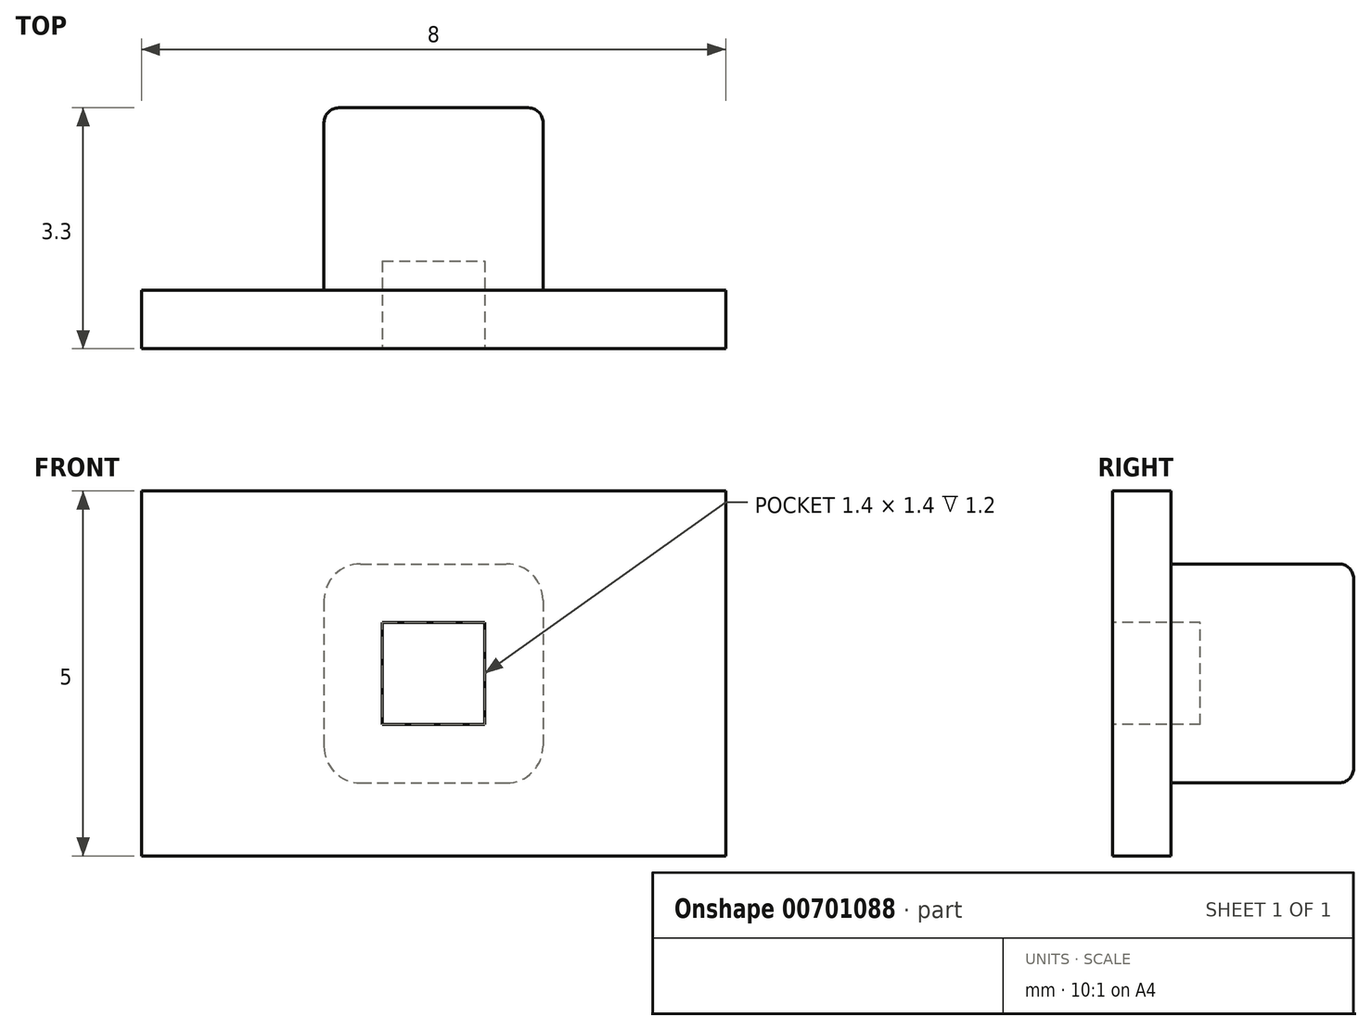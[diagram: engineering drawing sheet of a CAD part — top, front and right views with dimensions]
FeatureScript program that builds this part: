
annotation { "Feature Type Name" : "Feature", "Feature Type Description" : "" }
export const myFeature = defineFeature(function(context is Context, id is Id, definition is map)
    precondition{}
    {
        {
            var Q0;
            Q0=qCreatedBy(makeId("Top.planeOp"),FACE);
            var sketch = newSketch(context, id + "F0", { "sketchPlane" : qUnion([Q0])});
            skLineSegment(sketch, "E0.bottom", {"start": v(0, 0) * mm, "end": v(8, 0) * mm});
            skLineSegment(sketch, "E0.top", {"start": v(0, 0.8) * mm, "end": v(2.5, 0.8) * mm});
            skLineSegment(sketch, "E0.left", {"start": v(0, 0) * mm, "end": v(0, 0.8) * mm});
            skLineSegment(sketch, "E0.right", {"start": v(8, 0) * mm, "end": v(8, 0.8) * mm});
            skLineSegment(sketch, "E1", {"start": v(2.5, 0.8) * mm, "end": v(2.5, 3.3) * mm});
            skLineSegment(sketch, "E2", {"start": v(2.5, 3.3) * mm, "end": v(5.5, 3.3) * mm});
            skLineSegment(sketch, "E3", {"start": v(5.5, 3.3) * mm, "end": v(5.5, 0.8) * mm});
            skLineSegment(sketch, "E4.trimOffspring", {"start": v(5.5, 0.8) * mm, "end": v(8, 0.8) * mm});
            skSolve(sketch);
        }
        {
            var Q0;
            Q0 = qSketchRegion(id + "F0", true);
            extrude(context, id + "F1", {"entities" : qUnion([Q0]), "depth" : 3 * mm, "offsetDistance" : 25 * mm});
        }
        {
            var Q0;
            Q0=makeQuery(id+"F1.opExtrude","SWEPT_FACE",FACE,{"disambiguationData":[OSD([sQuery(id+"F0.wireOp",EDGE,"E0.bottom")])]});
            var sketch = newSketch(context, id + "F2", { "sketchPlane" : qUnion([Q0])});
            skLineSegment(sketch, "E5.bottom", {"start": v(3.3, 0.8) * mm, "end": v(4.7, 0.8) * mm});
            skLineSegment(sketch, "E5.top", {"start": v(3.3, 2.2) * mm, "end": v(4.7, 2.2) * mm});
            skLineSegment(sketch, "E5.left", {"start": v(3.3, 0.8) * mm, "end": v(3.3, 2.2) * mm});
            skLineSegment(sketch, "E5.right", {"start": v(4.7, 0.8) * mm, "end": v(4.7, 2.2) * mm});
            skLineSegment(sketch, "E6", {"start": v(0, 1.5) * mm, "end": v(1.82, 1.5) * mm, "construction": true});
            skLineSegment(sketch, "E7", {"start": v(4, 0) * mm, "end": v(4, 0.82) * mm, "construction": true});
            skSolve(sketch);
        }
        {
            var Q0;
            Q0 = qSketchRegion(id + "F2", true);
            extrude(context, id + "F3", {"entities" : qUnion([Q0]), "operationType" : NewBodyOperationType.REMOVE, "oppositeDirection" : true, "depth" : 1.2 * mm, "offsetDistance" : 25 * mm});
        }
        {
            var Q0;
            Q0=makeQuery(id+"F1.opExtrude","CAP_EDGE",EDGE,{"disambiguationData":[OSD([sQuery(id+"F0.wireOp",EDGE,"E3")])],"isStart":false});
            var Q1;
            Q1=makeQuery(id+"F1.opExtrude","CAP_EDGE",EDGE,{"disambiguationData":[OSD([sQuery(id+"F0.wireOp",EDGE,"E1")])],"isStart":false});
            var Q2;
            Q2=makeQuery(id+"F1.opExtrude","CAP_EDGE",EDGE,{"disambiguationData":[OSD([sQuery(id+"F0.wireOp",EDGE,"E1")])],"isStart":true});
            var Q3;
            Q3=makeQuery(id+"F1.opExtrude","CAP_EDGE",EDGE,{"disambiguationData":[OSD([sQuery(id+"F0.wireOp",EDGE,"E3")])],"isStart":true});
            fillet(context, id + "F4", {"entities" : qUnion([Q0, Q1, Q2, Q3]), "radius" : 0.5 * mm, "tangentPropagation" : true, "allowEdgeOverflow" : false});
        }
        {
            var Q0;
            Q0=makeQuery(id+"F1.opExtrude","CAP_EDGE",EDGE,{"disambiguationData":[OSD([sQuery(id+"F0.wireOp",EDGE,"E2")])],"isStart":false});
            var Q1;
            Q1=makeQuery(id+"F4.opFillet","BLEND_EDGE",EDGE,{"blendedFrom":[makeQuery(id+"F1.opExtrude","CAP_EDGE",EDGE,{"disambiguationData":[OSD([sQuery(id+"F0.wireOp",EDGE,"E3")])],"isStart":false}),makeQuery(id+"F1.opExtrude","SWEPT_FACE",FACE,{"disambiguationData":[OSD([sQuery(id+"F0.wireOp",EDGE,"E2")])]})],"blendedInto":[makeQuery(id+"F1.opExtrude","SWEPT_FACE",FACE,{"disambiguationData":[OSD([sQuery(id+"F0.wireOp",EDGE,"E2")])]})]});
            var Q2;
            Q2=makeQuery(id+"F1.opExtrude","SWEPT_EDGE",EDGE,{"disambiguationData":[OSD([sQuery(id+"F0.wireOp",EDGE,"E2"),sQuery(id+"F0.wireOp",EDGE,"E3")])]});
            var Q3;
            Q3=makeQuery(id+"F4.opFillet","BLEND_EDGE",EDGE,{"blendedFrom":[makeQuery(id+"F1.opExtrude","CAP_EDGE",EDGE,{"disambiguationData":[OSD([sQuery(id+"F0.wireOp",EDGE,"E3")])],"isStart":true}),makeQuery(id+"F1.opExtrude","SWEPT_FACE",FACE,{"disambiguationData":[OSD([sQuery(id+"F0.wireOp",EDGE,"E2")])]})],"blendedInto":[makeQuery(id+"F1.opExtrude","SWEPT_FACE",FACE,{"disambiguationData":[OSD([sQuery(id+"F0.wireOp",EDGE,"E2")])]})]});
            var Q4;
            Q4=makeQuery(id+"F1.opExtrude","CAP_EDGE",EDGE,{"disambiguationData":[OSD([sQuery(id+"F0.wireOp",EDGE,"E2")])],"isStart":true});
            var Q5;
            Q5=makeQuery(id+"F4.opFillet","BLEND_EDGE",EDGE,{"blendedFrom":[makeQuery(id+"F1.opExtrude","CAP_EDGE",EDGE,{"disambiguationData":[OSD([sQuery(id+"F0.wireOp",EDGE,"E1")])],"isStart":true}),makeQuery(id+"F1.opExtrude","SWEPT_FACE",FACE,{"disambiguationData":[OSD([sQuery(id+"F0.wireOp",EDGE,"E2")])]})],"blendedInto":[makeQuery(id+"F1.opExtrude","SWEPT_FACE",FACE,{"disambiguationData":[OSD([sQuery(id+"F0.wireOp",EDGE,"E2")])]})]});
            var Q6;
            Q6=makeQuery(id+"F1.opExtrude","SWEPT_EDGE",EDGE,{"disambiguationData":[OSD([sQuery(id+"F0.wireOp",EDGE,"E1"),sQuery(id+"F0.wireOp",EDGE,"E2")])]});
            var Q7;
            Q7=makeQuery(id+"F4.opFillet","BLEND_EDGE",EDGE,{"blendedFrom":[makeQuery(id+"F1.opExtrude","CAP_EDGE",EDGE,{"disambiguationData":[OSD([sQuery(id+"F0.wireOp",EDGE,"E1")])],"isStart":false}),makeQuery(id+"F1.opExtrude","SWEPT_FACE",FACE,{"disambiguationData":[OSD([sQuery(id+"F0.wireOp",EDGE,"E2")])]})],"blendedInto":[makeQuery(id+"F1.opExtrude","SWEPT_FACE",FACE,{"disambiguationData":[OSD([sQuery(id+"F0.wireOp",EDGE,"E2")])]})]});
            fillet(context, id + "F5", {"entities" : qUnion([Q0, Q1, Q2, Q3, Q4, Q5, Q6, Q7]), "radius" : 0.2 * mm, "tangentPropagation" : true, "allowEdgeOverflow" : false});
        }
        {
            var Q0;
            Q0=makeQuery(id+"F1.opExtrude","SWEPT_FACE",FACE,{"disambiguationData":[OSD([sQuery(id+"F0.wireOp",EDGE,"E0.right")])]});
            var sketch = newSketch(context, id + "F6", { "sketchPlane" : qUnion([Q0])});
            skLineSegment(sketch, "E8.bottom", {"start": v(0, 4) * mm, "end": v(0.8, 4) * mm});
            skLineSegment(sketch, "E8.top", {"start": v(0, -1) * mm, "end": v(0.8, -1) * mm});
            skLineSegment(sketch, "E8.left", {"start": v(0, 4) * mm, "end": v(0, 3) * mm});
            skLineSegment(sketch, "E8.right", {"start": v(0.8, 4) * mm, "end": v(0.8, 3) * mm});
            skLineSegment(sketch, "E9.0", {"start": v(0, 3) * mm, "end": v(0.8, 3) * mm});
            skLineSegment(sketch, "E10.0", {"start": v(0, 0) * mm, "end": v(0.8, 0) * mm});
            skLineSegment(sketch, "E11.trimOffspring", {"start": v(0, 0) * mm, "end": v(0, -1) * mm});
            skLineSegment(sketch, "E12.trimOffspring", {"start": v(0.8, 0) * mm, "end": v(0.8, -1) * mm});
            skSolve(sketch);
        }
        {
            var Q0;
            Q0 = qSketchRegion(id + "F6", true);
            var Q1;
            Q1=makeQuery(id+"F1.opExtrude","SWEPT_FACE",FACE,{"disambiguationData":[OSD([sQuery(id+"F0.wireOp",EDGE,"E0.left")])]});
            extrude(context, id + "F7", {"entities" : qUnion([Q0]), "operationType" : NewBodyOperationType.ADD, "endBound" : BoundingType.UP_TO_SURFACE, "oppositeDirection" : true, "depth" : 25 * mm, "endBoundEntityFace" : qUnion([Q1]), "offsetDistance" : 25 * mm});
        }
    });
